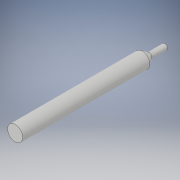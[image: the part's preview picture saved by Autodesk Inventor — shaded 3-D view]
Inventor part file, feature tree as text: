
AUTODESK INVENTOR PART (.ipt)
format: ipt  version: 2019 (Build 230136000, 136)  size: 116,736 bytes
history: native  units: mm
features: sketch x2, revolve x1, extrude x1
ambient origin geometry x8: Origin, YZ Plane, XZ Plane, XY Plane, X Axis, Y Axis, Z Axis, Center Point
bodies: Body1 (feature_tree)
feature tree (4):
  revolve  "Revolution2"  [1 undecoded]
  extrude  "Extrusion1"  Depth=250.0mm
  sketch  "Sketch1"  dims[d17=5.5mm d22=15.5mm]
  sketch  "Sketch2"  dims[d23=21.816616mm d24=5.0mm d25=13.613568mm d27=11.0mm d28=45.156946mm d29=90.0deg d30=15.0mm d31=30.0mm d32=250.0mm d33=0.0mm]
note: 1 required parameter value undecoded (feature->parameter linkage not recoverable at this tier; creation-order binding heuristic only, values carry confidence <= 0.55)
